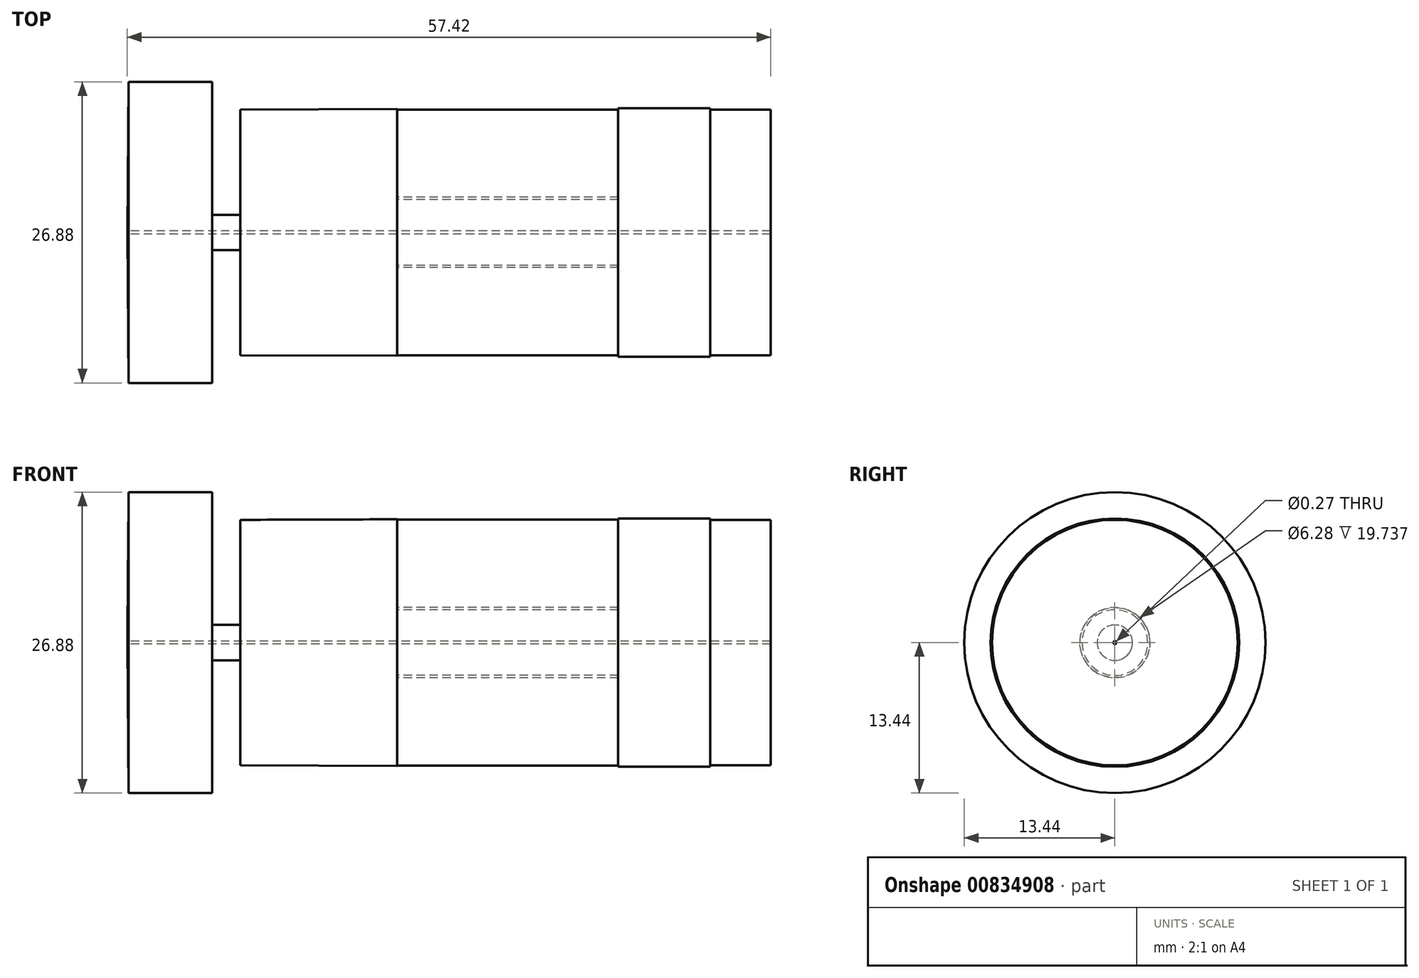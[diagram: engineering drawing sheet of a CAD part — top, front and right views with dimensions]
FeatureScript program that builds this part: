
annotation { "Feature Type Name" : "Feature", "Feature Type Description" : "" }
export const myFeature = defineFeature(function(context is Context, id is Id, definition is map)
    precondition{}
    {
        {
            var Q0;
            Q0=qCreatedBy(makeId("Front.planeOp"),FACE);
            var sketch = newSketch(context, id + "F0", { "sketchPlane" : qUnion([Q0])});
            skLineSegment(sketch, "E0.bottom", {"start": v(0, 0) * mm, "end": v(12.36, 0) * mm});
            skLineSegment(sketch, "E0.top", {"start": v(0, 26.86) * mm, "end": v(12.36, 26.86) * mm});
            skLineSegment(sketch, "E0.left", {"start": v(0, 13.43) * mm, "end": v(0, 26.86) * mm});
            skLineSegment(sketch, "E1", {"start": v(87, 25.7) * mm, "end": v(87, 13.43) * mm});
            skLineSegment(sketch, "E2", {"start": v(87, 0) * mm, "end": v(72.68, 4.73) * mm});
            skLineSegment(sketch, "E3", {"start": v(-54.05, 13.43) * mm, "end": v(89.4, 13.43) * mm, "construction": true});
            skLineSegment(sketch, "E4", {"start": v(72.68, 4.73) * mm, "end": v(72.68, 22.13) * mm});
            skLineSegment(sketch, "E5", {"start": v(72.68, 22.13) * mm, "end": v(87, 25.7) * mm});
            skLineSegment(sketch, "E6", {"start": v(72.68, 22.13) * mm, "end": v(72.68, 4.73) * mm});
            skLineSegment(sketch, "E7", {"start": v(12.36, 24.36) * mm, "end": v(64.66, 24.36) * mm});
            skLineSegment(sketch, "E8", {"start": v(64.66, 24.36) * mm, "end": v(64.66, 2.5) * mm});
            skLineSegment(sketch, "E9", {"start": v(64.66, 2.5) * mm, "end": v(12.36, 2.5) * mm});
            skLineSegment(sketch, "E10", {"start": v(64.66, 24.36) * mm, "end": v(72.68, 22.13) * mm});
            skLineSegment(sketch, "E11", {"start": v(64.66, 2.5) * mm, "end": v(72.68, 4.73) * mm});
            skLineSegment(sketch, "E12", {"start": v(12.36, 16.1) * mm, "end": v(64.66, 16.1) * mm});
            skLineSegment(sketch, "E13", {"start": v(12.36, 10.76) * mm, "end": v(64.66, 10.76) * mm});
            skLineSegment(sketch, "E14", {"start": v(23.72, 24.36) * mm, "end": v(23.72, 2.5) * mm});
            skLineSegment(sketch, "E15", {"start": v(57.31, 24.36) * mm, "end": v(57.31, 2.5) * mm});
            skLineSegment(sketch, "E16", {"start": v(49.89, 24.36) * mm, "end": v(49.89, 2.5) * mm});
            skLineSegment(sketch, "E17.trimOffspring", {"start": v(12.36, 24.36) * mm, "end": v(12.36, 26.86) * mm});
            skSolve(sketch);
        }
        {
            var Q0;
            Q0=qCreatedBy(makeId("Front.planeOp"),FACE);
            var sketch = newSketch(context, id + "F1", { "sketchPlane" : qUnion([Q0])});
            skLineSegment(sketch, "E18", {"start": v(7.47, 26.86) * mm, "end": v(14.94, 26.86) * mm});
            skLineSegment(sketch, "E19", {"start": v(14.94, 0) * mm, "end": v(0, 0) * mm});
            skLineSegment(sketch, "E20", {"start": v(14.94, 26.86) * mm, "end": v(17.44, 24.36) * mm});
            skLineSegment(sketch, "E21", {"start": v(17.44, 24.36) * mm, "end": v(64.66, 24.36) * mm});
            skLineSegment(sketch, "E22", {"start": v(64.66, 2.5) * mm, "end": v(17.44, 2.5) * mm});
            skLineSegment(sketch, "E23", {"start": v(72.68, 4.73) * mm, "end": v(64.66, 2.5) * mm});
            skLineSegment(sketch, "E24", {"start": v(64.66, 24.36) * mm, "end": v(72.68, 22.13) * mm});
            skLineSegment(sketch, "E25", {"start": v(72.68, 22.13) * mm, "end": v(87, 25.7) * mm});
            skLineSegment(sketch, "E26", {"start": v(87, 1.17) * mm, "end": v(72.68, 4.73) * mm});
            skLineSegment(sketch, "E27", {"start": v(-10.85, 13.43) * mm, "end": v(99.91, 13.43) * mm});
            skPoint(sketch, "E28.oppositeSnap0", {"position": v(7.47, 26.86) * mm});
            skLineSegment(sketch, "E28.bottom", {"start": v(14.94, 13.43) * mm, "end": v(7.47, 13.43) * mm});
            skLineSegment(sketch, "E28.top", {"start": v(14.94, 26.82) * mm, "end": v(7.47, 26.82) * mm});
            skLineSegment(sketch, "E28.left", {"start": v(14.94, 14.92) * mm, "end": v(14.94, 26.82) * mm});
            skLineSegment(sketch, "E28.right", {"start": v(7.47, 13.43) * mm, "end": v(7.47, 26.82) * mm});
            skLineSegment(sketch, "E29.bottom", {"start": v(18.58, 13.43) * mm, "end": v(31.45, 13.43) * mm});
            skLineSegment(sketch, "E29.top", {"start": v(18.58, 24.36) * mm, "end": v(31.45, 24.36) * mm});
            skLineSegment(sketch, "E29.left", {"start": v(18.58, 14.92) * mm, "end": v(18.58, 24.36) * mm});
            skLineSegment(sketch, "E29.right", {"start": v(31.45, 16.42) * mm, "end": v(31.45, 24.36) * mm});
            skLineSegment(sketch, "E30.bottom", {"start": v(31.45, 13.43) * mm, "end": v(51.29, 13.43) * mm});
            skLineSegment(sketch, "E30.top", {"start": v(31.45, 16.42) * mm, "end": v(51.29, 16.42) * mm});
            skLineSegment(sketch, "E31.bottom", {"start": v(51.29, 13.43) * mm, "end": v(59.44, 13.43) * mm});
            skLineSegment(sketch, "E31.top", {"start": v(51.29, 24.36) * mm, "end": v(59.44, 24.36) * mm});
            skLineSegment(sketch, "E31.left", {"start": v(51.29, 16.42) * mm, "end": v(51.29, 24.36) * mm});
            skLineSegment(sketch, "E31.right", {"start": v(59.44, 14.92) * mm, "end": v(59.44, 24.36) * mm});
            skLineSegment(sketch, "E32.bottom", {"start": v(59.44, 13.43) * mm, "end": v(64.66, 13.43) * mm});
            skLineSegment(sketch, "E32.top", {"start": v(59.44, 24.36) * mm, "end": v(64.66, 24.36) * mm});
            skLineSegment(sketch, "E32.right", {"start": v(64.66, 13.43) * mm, "end": v(64.66, 24.36) * mm});
            skLineSegment(sketch, "E33.top", {"start": v(31.45, 24.36) * mm, "end": v(51.29, 24.36) * mm});
            skLineSegment(sketch, "E34.bottom", {"start": v(14.94, 13.43) * mm, "end": v(59.44, 13.43) * mm});
            skLineSegment(sketch, "E34.top", {"start": v(14.94, 14.92) * mm, "end": v(59.44, 14.92) * mm});
            skPoint(sketch, "E35.orphan", {"position": v(0, 26.86) * mm});
            skSolve(sketch);
        }
        {
            var Q0;
            Q0=qCreatedBy(makeId("Front.planeOp"),FACE);
            var sketch = newSketch(context, id + "F2", { "sketchPlane" : qUnion([Q0])});
            skLineSegment(sketch, "E36", {"start": v(7.36, 13.56) * mm, "end": v(64.78, 13.56) * mm});
            skLineSegment(sketch, "E37", {"start": v(64.78, 13.56) * mm, "end": v(64.78, 24.4) * mm});
            skLineSegment(sketch, "E38", {"start": v(64.78, 24.4) * mm, "end": v(59.36, 24.4) * mm});
            skLineSegment(sketch, "E39", {"start": v(59.36, 24.4) * mm, "end": v(59.36, 15) * mm});
            skLineSegment(sketch, "E40", {"start": v(59.36, 15) * mm, "end": v(14.94, 15) * mm});
            skLineSegment(sketch, "E41", {"start": v(14.94, 15) * mm, "end": v(14.94, 26.87) * mm});
            skLineSegment(sketch, "E42", {"start": v(14.94, 26.87) * mm, "end": v(7.48, 26.87) * mm});
            skLineSegment(sketch, "E43", {"start": v(7.48, 26.87) * mm, "end": v(7.36, 13.56) * mm});
            skSolve(sketch);
        }
        {
            var Q0;
            Q0 = qSketchRegion(id + "F2", true);
            var Q1;
            Q1=sQuery(id+"F1.wireOp",EDGE,"E27");
            revolve(context, id + "F3", {"surfaceOperationType" : NewSurfaceOperationType.NEW, "entities" : qUnion([Q0]), "axis" : qUnion([Q1]), "revolveType" : RevolveType.FULL});
        }
        {
            var Q0;
            Q0=qCreatedBy(makeId("Front.planeOp"),FACE);
            var sketch = newSketch(context, id + "F4", { "sketchPlane" : qUnion([Q0])});
            skLineSegment(sketch, "E44", {"start": v(17.43, 24.4) * mm, "end": v(17.43, 15) * mm});
            skLineSegment(sketch, "E45", {"start": v(17.43, 15) * mm, "end": v(59.37, 15) * mm});
            skLineSegment(sketch, "E46", {"start": v(59.37, 15) * mm, "end": v(59.37, 24.52) * mm});
            skLineSegment(sketch, "E47", {"start": v(59.37, 24.52) * mm, "end": v(51.17, 24.52) * mm});
            skLineSegment(sketch, "E48", {"start": v(51.17, 24.52) * mm, "end": v(51.17, 16.36) * mm});
            skLineSegment(sketch, "E49", {"start": v(51.17, 16.36) * mm, "end": v(31.44, 16.36) * mm});
            skLineSegment(sketch, "E50", {"start": v(31.44, 16.36) * mm, "end": v(31.44, 24.44) * mm});
            skLineSegment(sketch, "E51", {"start": v(31.44, 24.44) * mm, "end": v(17.43, 24.4) * mm});
            skSolve(sketch);
        }
        {
            var Q0;
            Q0 = qSketchRegion(id + "F4", true);
            var Q1;
            Q1=sQuery(id+"F1.wireOp",EDGE,"E27");
            revolve(context, id + "F5", {"operationType" : NewBodyOperationType.ADD, "surfaceOperationType" : NewSurfaceOperationType.NEW, "entities" : qUnion([Q0]), "axis" : qUnion([Q1]), "revolveType" : RevolveType.FULL});
        }
        {
            var Q0;
            Q0=qCreatedBy(makeId("Front.planeOp"),FACE);
            var sketch = newSketch(context, id + "F6", { "sketchPlane" : qUnion([Q0])});
            skLineSegment(sketch, "E52.bottom", {"start": v(31.4, 16.57) * mm, "end": v(51.17, 16.57) * mm});
            skLineSegment(sketch, "E52.top", {"start": v(31.4, 24.4) * mm, "end": v(51.17, 24.4) * mm});
            skLineSegment(sketch, "E52.left", {"start": v(31.4, 16.57) * mm, "end": v(31.4, 24.4) * mm});
            skLineSegment(sketch, "E52.right", {"start": v(51.17, 16.57) * mm, "end": v(51.17, 24.4) * mm});
            skSolve(sketch);
        }
        {
            var Q0;
            Q0 = qSketchRegion(id + "F6", true);
            var Q1;
            Q1=sQuery(id+"F1.wireOp",EDGE,"E27");
            revolve(context, id + "F7", {"operationType" : NewBodyOperationType.ADD, "surfaceOperationType" : NewSurfaceOperationType.NEW, "entities" : qUnion([Q0]), "axis" : qUnion([Q1]), "revolveType" : RevolveType.FULL});
        }
        {
            var Q0;
            Q0=qCreatedBy(makeId("Front.planeOp"),FACE);
            var sketch = newSketch(context, id + "F8", { "sketchPlane" : qUnion([Q0])});
            skLineSegment(sketch, "E53", {"start": v(14.93, 26.9) * mm, "end": v(15.34, 26.41) * mm});
            skLineSegment(sketch, "E54", {"start": v(15.34, 26.41) * mm, "end": v(14.93, 26.41) * mm});
            skLineSegment(sketch, "E55", {"start": v(14.93, 26.41) * mm, "end": v(14.93, 24.56) * mm});
            skLineSegment(sketch, "E56", {"start": v(14.93, 24.56) * mm, "end": v(17.27, 24.56) * mm});
            skLineSegment(sketch, "E57", {"start": v(17.27, 24.56) * mm, "end": v(17.46, 24.37) * mm});
            skLineSegment(sketch, "E58", {"start": v(17.46, 24.37) * mm, "end": v(17.46, 14.94) * mm});
            skLineSegment(sketch, "E59", {"start": v(14.93, 14.94) * mm, "end": v(14.93, 26.9) * mm});
            skSolve(sketch);
        }
        {
            var Q0;
            Q0 = qSketchRegion(id + "F8", true);
            var Q1;
            Q1=sQuery(id+"F8.wireOp",EDGE,"E53");
            var Q2;
            Q2=sQuery(id+"F8.wireOp",EDGE,"E54");
            var Q3;
            Q3=sQuery(id+"F8.wireOp",EDGE,"E55");
            var Q4;
            Q4=sQuery(id+"F8.wireOp",EDGE,"E56");
            var Q5;
            Q5=sQuery(id+"F8.wireOp",EDGE,"E57");
            var Q6;
            Q6=sQuery(id+"F1.wireOp",EDGE,"E29.bottom");
            revolve(context, id + "F9", {"bodyType" : ToolBodyType.SURFACE, "surfaceOperationType" : NewSurfaceOperationType.NEW, "entities" : qUnion([Q0]), "surfaceEntities" : qUnion([Q1, Q2, Q3, Q4, Q5]), "axis" : qUnion([Q6]), "revolveType" : RevolveType.FULL});
        }
    });
